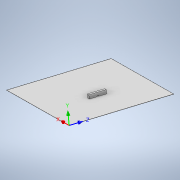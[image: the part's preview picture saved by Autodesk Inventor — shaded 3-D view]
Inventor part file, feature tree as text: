
AUTODESK INVENTOR PART (.ipt)
format: ipt  version: 2021 (Build 250183000, 183)  size: 128,000 bytes
history: native  units: mm
features: other x9, sketch x3, extrude x3
ambient origin geometry x8: Origin, YZ Plane, XZ Plane, XY Plane, X Axis, Y Axis, Z Axis, Center Point
bodies: Body1 (feature_tree), Body2 (feature_tree)
feature tree (15):
  sketch  "Boceto8"  dims[d42=480000.0mm d43=480000.0mm]
  extrude  "Extrusión7"  Depth=480000.0mm
  extrude  "Extrusión8"  Depth=80000.0mm
  other  "SCU1"
  extrude  "Extrusión9"  Depth=6000.0mm
  sketch  "Boceto9"  dims[d44=12000.0mm d45=80000.0mm]
  sketch  "Boceto10"  dims[d47=18000.0mm d48=0.0mm d49=6000.0mm d50=4000.0mm d51=0.0mm d52=0.0mm d53=0.0mm d54=0.0mm d55=0.0mm d56=0.0mm d57=0.0mm d58=0.0mm d59=1000.0mm d60=0.0mm d61=180000.0mm d40=500.0mm d41=0.872665mm]
  other  "Sólido6"
  other  "SCU1: Plano YZ"
  other  "SCU1: Plano XZ"
  other  "SCU1: Plano XY"
  other  "SCU1: Eje X"
  other  "SCU1: Eje Y"
  other  "SCU1: Eje Z"
  other  "SCU1: Centro"
